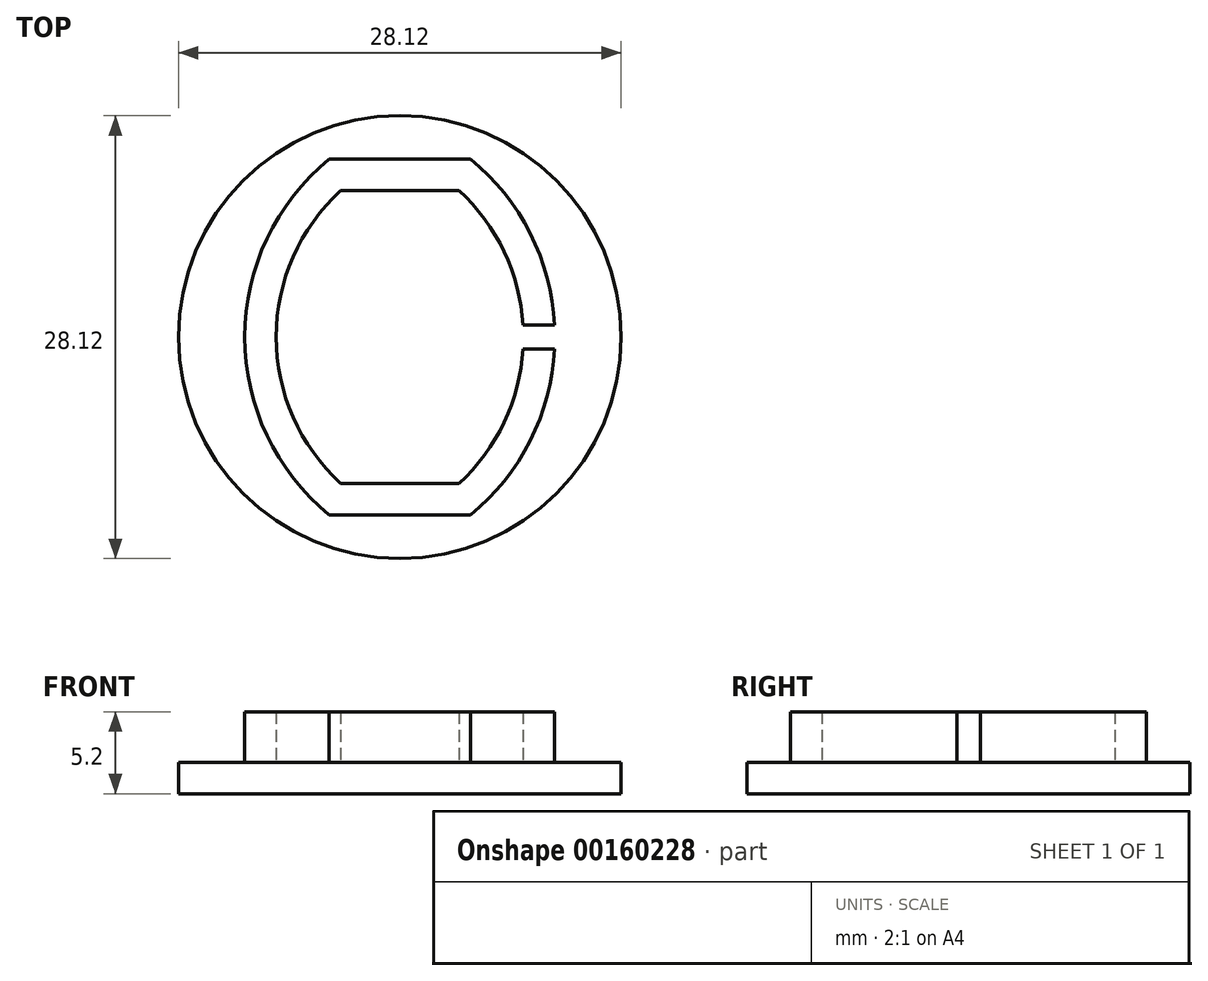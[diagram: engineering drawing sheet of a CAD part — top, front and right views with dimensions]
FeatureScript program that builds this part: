
annotation { "Feature Type Name" : "Feature", "Feature Type Description" : "" }
export const myFeature = defineFeature(function(context is Context, id is Id, definition is map)
    precondition{}
    {
        {
            var Q0;
            Q0=qCreatedBy(makeId("Top.planeOp"),FACE);
            var sketch = newSketch(context, id + "F0", { "sketchPlane" : qUnion([Q0])});
            skLineSegment(sketch, "E0", {"start": v(-5.09, 10.04) * mm, "end": v(2.41, 10.04) * mm});
            skLineSegment(sketch, "E1", {"start": v(-5.09, -8.56) * mm, "end": v(2.41, -8.56) * mm});
            skArc(sketch, "E2", {"start": v(2.41, -8.56) * mm, "mid": v(5.29, -4.68) * mm, "end": v(6.5, 0) * mm});
            skArc(sketch, "E3", {"start": v(-5.09, 10.04) * mm, "mid": v(-9.19, 0.74) * mm, "end": v(-5.09, -8.56) * mm});
            skArc(sketch, "E4.0", {"start": v(-5.83, 12.04) * mm, "mid": v(-11.19, 0.74) * mm, "end": v(-5.83, -10.56) * mm});
            skLineSegment(sketch, "E4.1", {"start": v(-5.83, 12.04) * mm, "end": v(3.16, 12.04) * mm});
            skArc(sketch, "E4.2", {"start": v(3.16, -10.56) * mm, "mid": v(6.94, -5.85) * mm, "end": v(8.5, 0) * mm});
            skLineSegment(sketch, "E4.3", {"start": v(-5.83, -10.56) * mm, "end": v(3.16, -10.56) * mm});
            skLineSegment(sketch, "E5", {"start": v(6.5, 1.5) * mm, "end": v(8.5, 1.5) * mm});
            skLineSegment(sketch, "E6", {"start": v(6.5, 0) * mm, "end": v(8.5, 0) * mm});
            skArc(sketch, "E7.trimOffspring", {"start": v(8.5, 1.5) * mm, "mid": v(6.94, 7.33) * mm, "end": v(3.16, 12.04) * mm});
            skArc(sketch, "E8.trimOffspring", {"start": v(6.5, 1.5) * mm, "mid": v(5.29, 6.17) * mm, "end": v(2.41, 10.04) * mm});
            skSolve(sketch);
        }
        {
            var Q0;
            Q0 = qSketchRegion(id + "F0", true);
            extrude(context, id + "F1", {"entities" : qUnion([Q0]), "depth" : 3.2 * mm});
        }
        {
            var Q0;
            Q0=qCreatedBy(makeId("Top.planeOp"),FACE);
            var sketch = newSketch(context, id + "F2", { "sketchPlane" : qUnion([Q0])});
            skCircle(sketch, "E9", {"center": v(-1.34, 0.74) * mm, "radius": 14.06 * mm});
            skLineSegment(sketch, "E10", {"start": v(-1.34, 12.04) * mm, "end": v(-1.34, -10.56) * mm, "construction": true});
            skLineSegment(sketch, "E11", {"start": v(-11.19, 0.74) * mm, "end": v(10.08, 0.74) * mm, "construction": true});
            skSolve(sketch);
        }
        {
            var Q0;
            Q0 = qSketchRegion(id + "F2", true);
            extrude(context, id + "F3", {"entities" : qUnion([Q0]), "operationType" : NewBodyOperationType.ADD, "oppositeDirection" : true, "depth" : 2 * mm});
        }
    });
